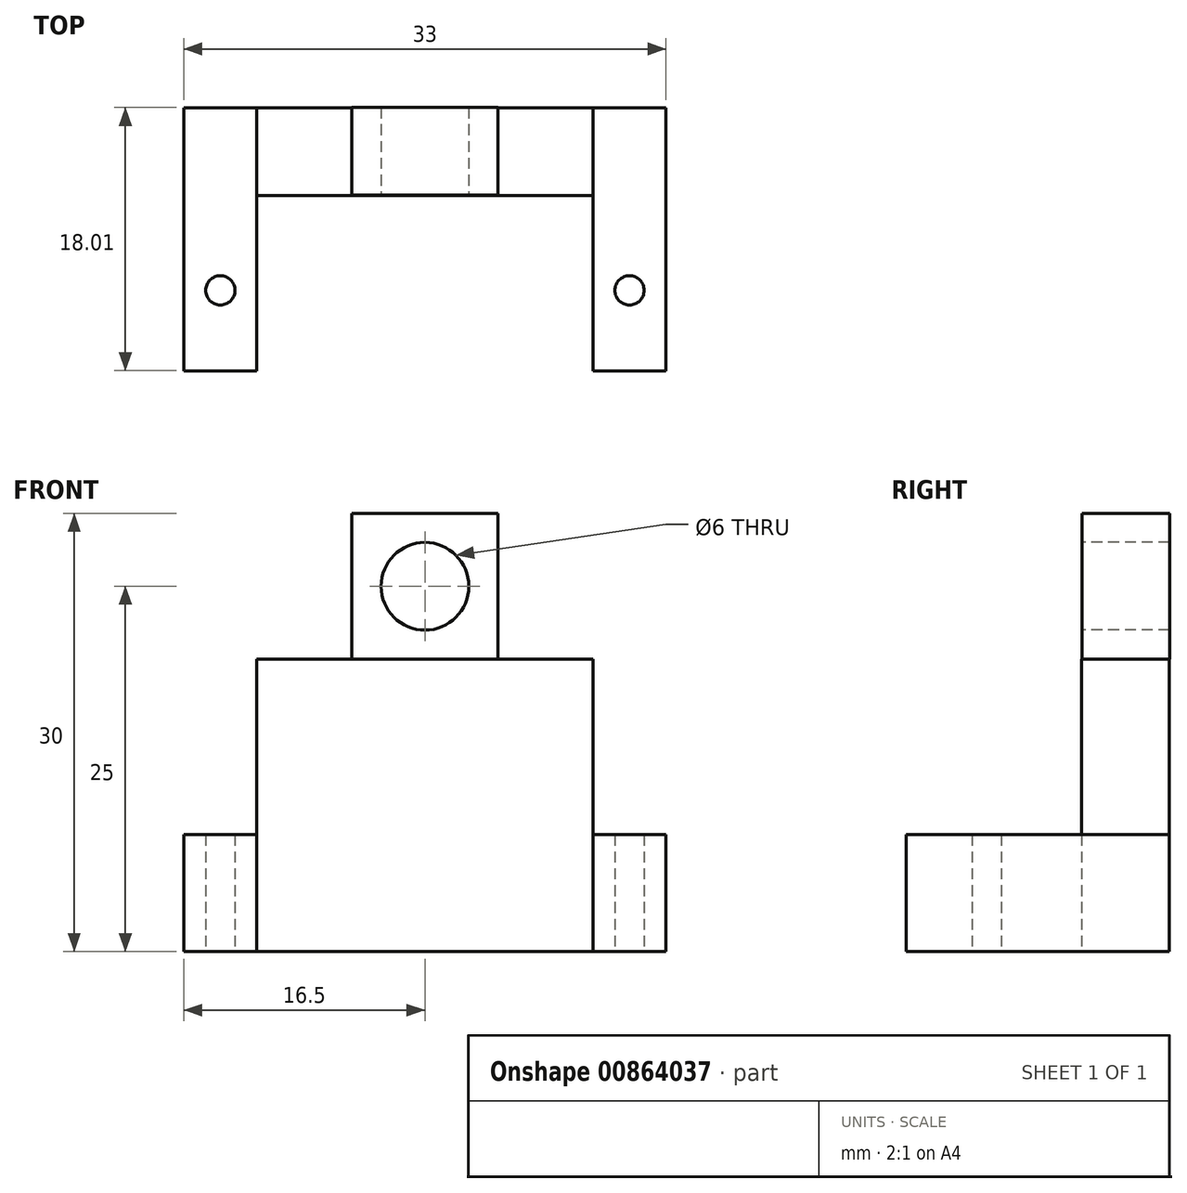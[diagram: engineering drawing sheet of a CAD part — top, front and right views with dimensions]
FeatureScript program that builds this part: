
annotation { "Feature Type Name" : "Feature", "Feature Type Description" : "" }
export const myFeature = defineFeature(function(context is Context, id is Id, definition is map)
    precondition{}
    {
        {
            var Q0;
            Q0=qCreatedBy(makeId("Top.planeOp"),FACE);
            var sketch = newSketch(context, id + "F0", { "sketchPlane" : qUnion([Q0])});
            skLineSegment(sketch, "E0.bottom", {"start": v(11.5, 7.79) * mm, "end": v(-11.5, 7.79) * mm});
            skLineSegment(sketch, "E0.top", {"start": v(11.5, 1.79) * mm, "end": v(-11.5, 1.79) * mm});
            skLineSegment(sketch, "E0.left", {"start": v(11.5, 7.79) * mm, "end": v(11.5, 1.79) * mm});
            skLineSegment(sketch, "E0.right", {"start": v(-11.5, 7.79) * mm, "end": v(-11.5, 1.79) * mm});
            skLineSegment(sketch, "E1.bottom", {"start": v(-11.5, 7.79) * mm, "end": v(-16.5, 7.79) * mm});
            skLineSegment(sketch, "E1.top", {"start": v(-11.5, -10.21) * mm, "end": v(-16.5, -10.21) * mm});
            skLineSegment(sketch, "E1.left", {"start": v(-11.5, 7.79) * mm, "end": v(-11.5, -10.21) * mm});
            skLineSegment(sketch, "E1.right", {"start": v(-16.5, 7.79) * mm, "end": v(-16.5, -10.21) * mm});
            skLineSegment(sketch, "E2.bottom", {"start": v(11.5, 7.79) * mm, "end": v(16.5, 7.79) * mm});
            skLineSegment(sketch, "E2.top", {"start": v(11.5, -10.21) * mm, "end": v(16.5, -10.21) * mm});
            skLineSegment(sketch, "E2.left", {"start": v(11.5, 7.79) * mm, "end": v(11.5, -10.21) * mm});
            skLineSegment(sketch, "E2.right", {"start": v(16.5, 7.79) * mm, "end": v(16.5, -10.21) * mm});
            skCircle(sketch, "E3", {"center": v(-14, -4.71) * mm, "radius": 1 * mm});
            skCircle(sketch, "E4", {"center": v(14, -4.71) * mm, "radius": 1 * mm});
            skSolve(sketch);
        }
        {
            var Q0;
            {var subQ3=sQuery(id+"F0.wireOp",EDGE,"E1.bottom");Q0=makeQuery(id+"F0.imprint","IMPRINT",FACE,{"disambiguationData":[TD([[makeQuery(id+"F0.imprint","IMPRINT",EDGE,{"derivedFrom":subQ3}),1.0]])]});}
            var Q1;
            {var subQ3=sQuery(id+"F0.wireOp",EDGE,"E2.bottom");Q1=makeQuery(id+"F0.imprint","IMPRINT",FACE,{"disambiguationData":[TD([[makeQuery(id+"F0.imprint","IMPRINT",EDGE,{"derivedFrom":subQ3}),-1.0]])]});}
            extrude(context, id + "F1", {"entities" : qUnion([Q0, Q1]), "offsetDistance" : 25 * mm, "depth" : 8 * mm});
        }
        {
            var Q0;
            {var subQ0=sQuery(id+"F0.wireOp",EDGE,"E0.bottom");Q0=makeQuery(id+"F0.imprint","IMPRINT",FACE,{"disambiguationData":[TD([[makeQuery(id+"F0.imprint","IMPRINT",EDGE,{"derivedFrom":subQ0}),1.0]])]});}
            extrude(context, id + "F2", {"entities" : qUnion([Q0]), "operationType" : NewBodyOperationType.ADD, "offsetDistance" : 25 * mm, "depth" : 20 * mm});
        }
        {
            var Q0;
            Q0=qCreatedBy(makeId("Front.planeOp"),FACE);
            var sketch = newSketch(context, id + "F3", { "sketchPlane" : qUnion([Q0])});
            skPoint(sketch, "E5", {"position": v(0, 20) * mm});
            skPoint(sketch, "E6", {"position": v(0, 30) * mm});
            skPoint(sketch, "E7", {"position": v(0, 25) * mm});
            skPoint(sketch, "E8", {"position": v(5, 30) * mm});
            skPoint(sketch, "E9", {"position": v(-5, 20) * mm});
            skLineSegment(sketch, "E10.bottom", {"start": v(-5, 20) * mm, "end": v(5, 20) * mm});
            skLineSegment(sketch, "E10.top", {"start": v(-5, 30) * mm, "end": v(5, 30) * mm});
            skLineSegment(sketch, "E10.left", {"start": v(-5, 20) * mm, "end": v(-5, 30) * mm});
            skLineSegment(sketch, "E10.right", {"start": v(5, 20) * mm, "end": v(5, 30) * mm});
            skCircle(sketch, "E11", {"center": v(0, 25) * mm, "radius": 3 * mm});
            skSolve(sketch);
        }
        {
            var Q0;
            Q0=makeQuery(id+"F3.imprint","IMPRINT",FACE,{"disambiguationData":[TD([[makeQuery(id+"F3.imprint","IMPRINT",EDGE,{"derivedFrom":sQuery(id+"F3.wireOp",EDGE,"E10.bottom")}),1.0]])]});
            extrude(context, id + "F4", {"entities" : qUnion([Q0]), "operationType" : NewBodyOperationType.ADD, "oppositeDirection" : true, "depth" : 7.8 * mm, "offsetDistance" : 25 * mm, "hasSecondDirection" : true, "secondDirectionOppositeDirection" : true, "secondDirectionDepth" : 1.8 * mm});
        }
    });
